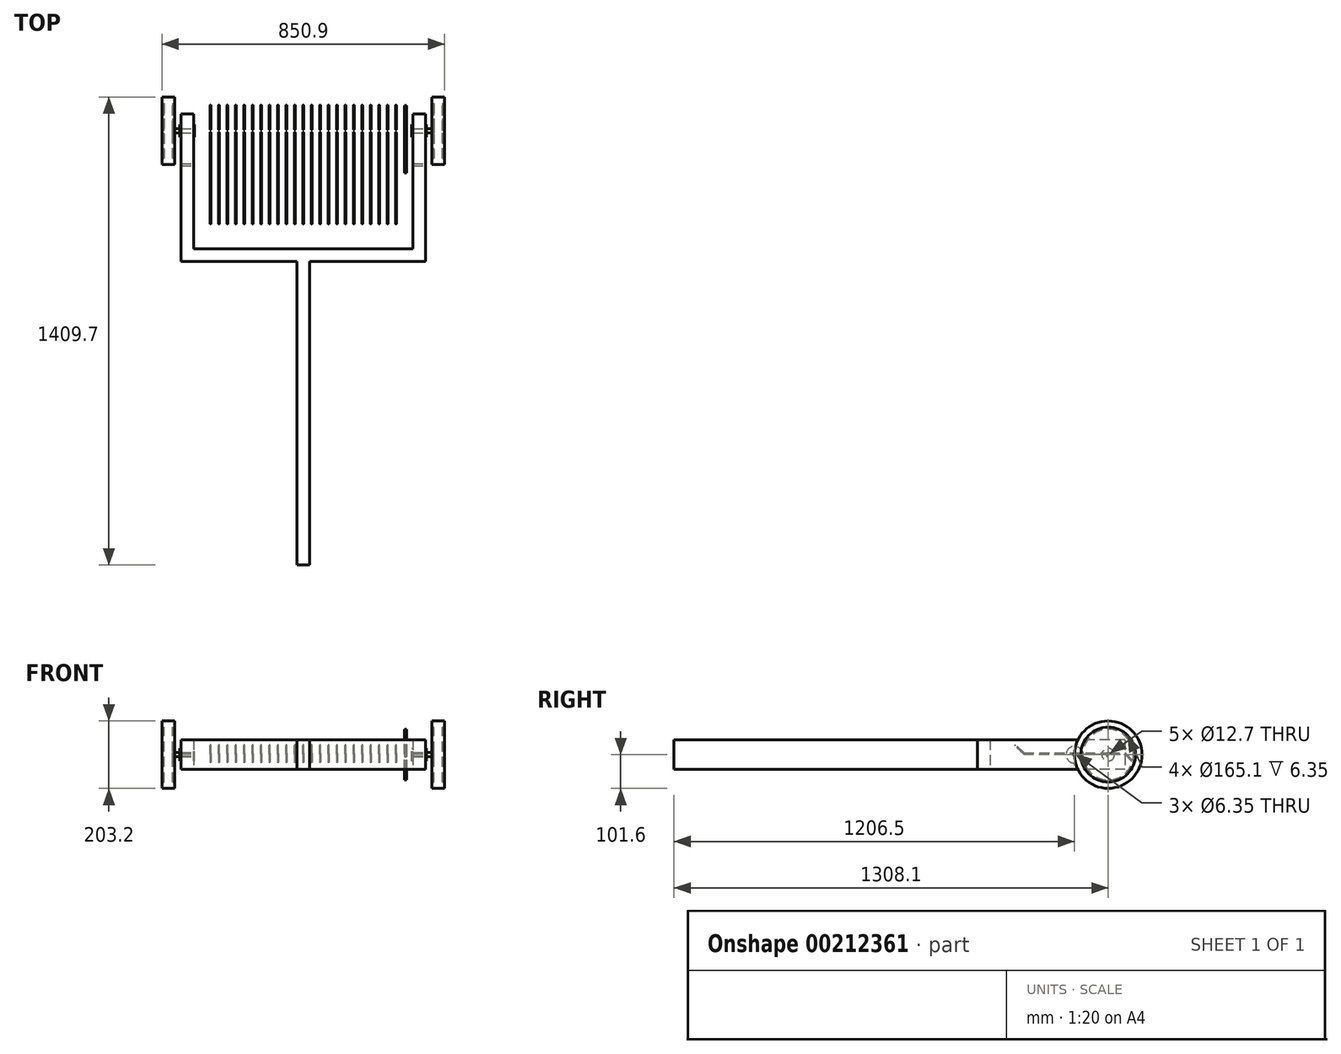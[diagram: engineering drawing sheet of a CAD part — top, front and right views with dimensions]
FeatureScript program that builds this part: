
annotation { "Feature Type Name" : "Feature", "Feature Type Description" : "" }
export const myFeature = defineFeature(function(context is Context, id is Id, definition is map)
    precondition{}
    {
        {
            var Q0;
            Q0=qCreatedBy(makeId("Top.planeOp"),FACE);
            var sketch = newSketch(context, id + "F0", { "sketchPlane" : qUnion([Q0])});
            skLineSegment(sketch, "E0.bottom", {"start": v(-368.3, 152.4) * mm, "end": v(-330.2, 152.4) * mm});
            skLineSegment(sketch, "E0.top", {"start": v(-368.3, -292.1) * mm, "end": v(-19.05, -292.1) * mm});
            skLineSegment(sketch, "E0.left", {"start": v(-368.3, 152.4) * mm, "end": v(-368.3, -292.1) * mm});
            skLineSegment(sketch, "E0.right", {"start": v(368.3, 152.4) * mm, "end": v(368.3, -292.1) * mm});
            skLineSegment(sketch, "E1.top", {"start": v(-19.05, -1206.5) * mm, "end": v(19.05, -1206.5) * mm});
            skLineSegment(sketch, "E1.left", {"start": v(-19.05, -292.1) * mm, "end": v(-19.05, -1206.5) * mm});
            skLineSegment(sketch, "E1.right", {"start": v(19.05, -292.1) * mm, "end": v(19.05, -1206.5) * mm});
            skLineSegment(sketch, "E2.top", {"start": v(-330.2, -254) * mm, "end": v(330.2, -254) * mm});
            skLineSegment(sketch, "E2.left", {"start": v(-330.2, 152.4) * mm, "end": v(-330.2, -254) * mm});
            skLineSegment(sketch, "E2.right", {"start": v(330.2, 152.4) * mm, "end": v(330.2, -254) * mm});
            skLineSegment(sketch, "E3.trimOffspring", {"start": v(330.2, 152.4) * mm, "end": v(368.3, 152.4) * mm});
            skLineSegment(sketch, "E4.trimOffspring", {"start": v(19.05, -292.1) * mm, "end": v(368.3, -292.1) * mm});
            skLineSegment(sketch, "E5", {"start": v(19.05, -292.1) * mm, "end": v(19.05, -254) * mm, "construction": true});
            skLineSegment(sketch, "E6", {"start": v(0, 0) * mm, "end": v(0, -254) * mm, "construction": true});
            skSolve(sketch);
        }
        {
            var Q0;
            Q0 = qSketchRegion(id + "F0", true);
            extrude(context, id + "F1", {"entities" : qUnion([Q0]), "endBound" : BoundingType.SYMMETRIC, "depth" : 88.9 * mm});
        }
        {
            var Q0;
            Q0=qCreatedBy(makeId("Right.planeOp"),FACE);
            var sketch = newSketch(context, id + "F2", { "sketchPlane" : qUnion([Q0])});
            skCircle(sketch, "E7", {"center": v(0, 0) * mm, "radius": 3.17 * mm});
            skSolve(sketch);
        }
        {
            var Q0;
            Q0 = qSketchRegion(id + "F2", true);
            extrude(context, id + "F3", {"entities" : qUnion([Q0]), "endBound" : BoundingType.SYMMETRIC, "depth" : 711.2 * mm});
        }
        {
            var Q0;
            Q0=qCreatedBy(makeId("Right.planeOp"),FACE);
            var sketch = newSketch(context, id + "F4", { "sketchPlane" : qUnion([Q0])});
            skLineSegment(sketch, "E8", {"start": v(-152.4, 3.17) * mm, "end": v(0, 3.17) * mm, "construction": true});
            skLineSegment(sketch, "E9", {"start": v(152.4, 3.17) * mm, "end": v(177.8, -22.22) * mm});
            skLineSegment(sketch, "E10", {"start": v(-152.4, 3.17) * mm, "end": v(-177.8, 28.58) * mm, "construction": true});
            skLineSegment(sketch, "E11", {"start": v(0, 0) * mm, "end": v(0, 3.17) * mm, "construction": true});
            skCircle(sketch, "E12.0", {"center": v(0, 0) * mm, "radius": 3.17 * mm, "construction": true});
            skLineSegment(sketch, "E13", {"start": v(-177.8, 28.58) * mm, "end": v(0, 3.17) * mm, "construction": true});
            skLineSegment(sketch, "E14", {"start": v(0, 3.17) * mm, "end": v(177.8, -22.22) * mm, "construction": true});
            skLineSegment(sketch, "E15", {"start": v(0, 3.17) * mm, "end": v(152.4, 3.17) * mm});
            skSolve(sketch);
        }
        {
            var Q0;
            Q0=qCreatedBy(makeId("Front.planeOp"),FACE);
            var sketch = newSketch(context, id + "F5", { "sketchPlane" : qUnion([Q0])});
            skCircle(sketch, "E16", {"center": v(0, 3.17) * mm, "radius": 1.59 * mm});
            skCircle(sketch, "E17.1.0.0", {"center": v(25.4, 3.17) * mm, "radius": 1.59 * mm});
            skCircle(sketch, "E17.2.0.0", {"center": v(50.8, 3.17) * mm, "radius": 1.59 * mm});
            skCircle(sketch, "E17.3.0.0", {"center": v(76.2, 3.17) * mm, "radius": 1.59 * mm});
            skCircle(sketch, "E17.4.0.0", {"center": v(101.6, 3.17) * mm, "radius": 1.59 * mm});
            skCircle(sketch, "E17.5.0.0", {"center": v(127, 3.17) * mm, "radius": 1.59 * mm});
            skCircle(sketch, "E17.6.0.0", {"center": v(152.4, 3.17) * mm, "radius": 1.59 * mm});
            skCircle(sketch, "E17.7.0.0", {"center": v(177.8, 3.17) * mm, "radius": 1.59 * mm});
            skCircle(sketch, "E17.8.0.0", {"center": v(203.2, 3.17) * mm, "radius": 1.59 * mm});
            skCircle(sketch, "E17.9.0.0", {"center": v(228.6, 3.17) * mm, "radius": 1.59 * mm});
            skCircle(sketch, "E17.10.0.0", {"center": v(254, 3.17) * mm, "radius": 1.59 * mm});
            skCircle(sketch, "E17.11.0.0", {"center": v(279.4, 3.17) * mm, "radius": 1.59 * mm});
            skLineSegment(sketch, "E17.direction1", {"start": v(0, 3.17) * mm, "end": v(25.4, 3.17) * mm, "construction": true});
            skCircle(sketch, "E18.1.0.0", {"center": v(-25.4, 3.17) * mm, "radius": 1.59 * mm});
            skCircle(sketch, "E18.2.0.0", {"center": v(-50.8, 3.17) * mm, "radius": 1.59 * mm});
            skCircle(sketch, "E18.3.0.0", {"center": v(-76.2, 3.17) * mm, "radius": 1.59 * mm});
            skCircle(sketch, "E18.4.0.0", {"center": v(-101.6, 3.17) * mm, "radius": 1.59 * mm});
            skCircle(sketch, "E18.5.0.0", {"center": v(-127, 3.17) * mm, "radius": 1.59 * mm});
            skCircle(sketch, "E18.6.0.0", {"center": v(-152.4, 3.17) * mm, "radius": 1.59 * mm});
            skCircle(sketch, "E18.7.0.0", {"center": v(-177.8, 3.17) * mm, "radius": 1.59 * mm});
            skCircle(sketch, "E18.8.0.0", {"center": v(-203.2, 3.17) * mm, "radius": 1.59 * mm});
            skCircle(sketch, "E18.9.0.0", {"center": v(-228.6, 3.17) * mm, "radius": 1.59 * mm});
            skCircle(sketch, "E18.10.0.0", {"center": v(-254, 3.17) * mm, "radius": 1.59 * mm});
            skCircle(sketch, "E18.11.0.0", {"center": v(-279.4, 3.17) * mm, "radius": 1.59 * mm});
            skLineSegment(sketch, "E18.direction1", {"start": v(0, 3.17) * mm, "end": v(-25.4, 3.17) * mm, "construction": true});
            skSolve(sketch);
        }
        {
            var Q0;
            Q0 = qSketchRegion(id + "F5", true);
            var Q1;
            Q1 = qConstructionFilter(qBodyType(qCreatedBy(id + "F4" ,EDGE), BodyType.WIRE), ConstructionObject.NO);
            sweep(context, id + "F6", {"operationType" : NewBodyOperationType.ADD, "profiles" : qUnion([Q0]), "path" : qUnion([Q1])});
        }
        {
            var Q0;
            Q0=qCreatedBy(makeId("Right.planeOp"),FACE);
            var sketch = newSketch(context, id + "F7", { "sketchPlane" : qUnion([Q0])});
            skLineSegment(sketch, "E19.0", {"start": v(-152.4, 3.17) * mm, "end": v(0, 3.17) * mm});
            skLineSegment(sketch, "E20.0", {"start": v(-152.4, 3.17) * mm, "end": v(-177.8, 28.58) * mm});
            skSolve(sketch);
        }
        {
            var Q0;
            Q0 = qSketchRegion(id + "F5", true);
            var Q1;
            Q1 = qConstructionFilter(qBodyType(qCreatedBy(id + "F7" ,EDGE), BodyType.WIRE), ConstructionObject.NO);
            sweep(context, id + "F8", {"operationType" : NewBodyOperationType.ADD, "profiles" : qUnion([Q0]), "path" : qUnion([Q1])});
        }
        {
            var Q0;
            Q0=qCreatedBy(makeId("Front.planeOp"),FACE);
            cPlane(context, id + "F9", {"entities" : qUnion([Q0]), "cplaneType" : CPlaneType.OFFSET, "offset" : 101.6 * mm, "oppositeDirection" : true, "width" : 152.4 * mm, "height" : 152.4 * mm});
        }
        {
            var Q0;
            Q0=qCreatedBy(id+"F9.planeOp",FACE);
            var sketch = newSketch(context, id + "F10", { "sketchPlane" : qUnion([Q0])});
            skLineSegment(sketch, "E21", {"start": v(419.1, 0) * mm, "end": v(-419.1, 0) * mm, "construction": true});
            skLineSegment(sketch, "E22", {"start": v(0, 0) * mm, "end": v(0, 115.83) * mm, "construction": true});
            skLineSegment(sketch, "E23.0", {"start": v(368.3, 44.45) * mm, "end": v(368.3, -44.45) * mm, "construction": true});
            skLineSegment(sketch, "E24.bottom", {"start": v(425.45, 101.6) * mm, "end": v(387.35, 101.6) * mm});
            skLineSegment(sketch, "E24.top", {"start": v(425.45, 82.55) * mm, "end": v(419.1, 82.55) * mm});
            skLineSegment(sketch, "E24.left", {"start": v(425.45, 101.6) * mm, "end": v(425.45, 82.55) * mm});
            skLineSegment(sketch, "E24.right", {"start": v(387.35, 101.6) * mm, "end": v(387.35, 82.55) * mm});
            skLineSegment(sketch, "E25.bottom", {"start": v(419.1, 0) * mm, "end": v(393.7, 0) * mm});
            skLineSegment(sketch, "E25.left", {"start": v(419.1, 0) * mm, "end": v(419.1, 82.55) * mm});
            skLineSegment(sketch, "E25.right", {"start": v(393.7, 6.35) * mm, "end": v(393.7, 82.55) * mm});
            skLineSegment(sketch, "E26.trimOffspring", {"start": v(393.7, 82.55) * mm, "end": v(387.35, 82.55) * mm});
            skLineSegment(sketch, "E27.MirrorCS", {"start": v(-425.45, 82.55) * mm, "end": v(-419.1, 82.55) * mm});
            skLineSegment(sketch, "E28.MirrorCS", {"start": v(-393.7, 82.55) * mm, "end": v(-387.35, 82.55) * mm});
            skLineSegment(sketch, "E29.MirrorCS", {"start": v(-419.1, 0) * mm, "end": v(-393.7, 0) * mm});
            skLineSegment(sketch, "E30.MirrorCS", {"start": v(-393.7, 6.35) * mm, "end": v(-393.7, 82.55) * mm});
            skLineSegment(sketch, "E31.MirrorCS", {"start": v(-387.35, 101.6) * mm, "end": v(-387.35, 82.55) * mm});
            skLineSegment(sketch, "E32.MirrorCS", {"start": v(-425.45, 101.6) * mm, "end": v(-387.35, 101.6) * mm});
            skLineSegment(sketch, "E33.MirrorCS", {"start": v(-425.45, 101.6) * mm, "end": v(-425.45, 82.55) * mm});
            skLineSegment(sketch, "E34.MirrorCS", {"start": v(-419.1, 0) * mm, "end": v(-419.1, 82.55) * mm});
            skLineSegment(sketch, "E35.bottom", {"start": v(393.7, 0) * mm, "end": v(304.8, 0) * mm});
            skLineSegment(sketch, "E35.top", {"start": v(393.7, 6.35) * mm, "end": v(371.47, 6.35) * mm});
            skLineSegment(sketch, "E35.right", {"start": v(304.8, 0) * mm, "end": v(304.8, 6.35) * mm});
            skLineSegment(sketch, "E36.top", {"start": v(371.47, 19.05) * mm, "end": v(368.3, 19.05) * mm});
            skLineSegment(sketch, "E36.left", {"start": v(371.47, 6.35) * mm, "end": v(371.47, 19.05) * mm});
            skLineSegment(sketch, "E36.right", {"start": v(368.3, 6.35) * mm, "end": v(368.3, 19.05) * mm});
            skLineSegment(sketch, "E37.top", {"start": v(330.2, 19.05) * mm, "end": v(327.03, 19.05) * mm});
            skLineSegment(sketch, "E37.left", {"start": v(330.2, 6.35) * mm, "end": v(330.2, 19.05) * mm});
            skLineSegment(sketch, "E37.right", {"start": v(327.03, 6.35) * mm, "end": v(327.03, 19.05) * mm});
            skLineSegment(sketch, "E38.trimOffspring", {"start": v(327.03, 6.35) * mm, "end": v(304.8, 6.35) * mm});
            skLineSegment(sketch, "E39.trimOffspring", {"start": v(368.3, 6.35) * mm, "end": v(330.2, 6.35) * mm});
            skLineSegment(sketch, "E40.MirrorCS", {"start": v(-371.47, 19.05) * mm, "end": v(-368.3, 19.05) * mm});
            skLineSegment(sketch, "E41.MirrorCS", {"start": v(-304.8, 0) * mm, "end": v(-304.8, 6.35) * mm});
            skLineSegment(sketch, "E42.MirrorCS", {"start": v(-330.2, 19.05) * mm, "end": v(-327.03, 19.05) * mm});
            skLineSegment(sketch, "E43.MirrorCS", {"start": v(-368.3, 6.35) * mm, "end": v(-368.3, 19.05) * mm});
            skLineSegment(sketch, "E44.MirrorCS", {"start": v(-393.7, 6.35) * mm, "end": v(-371.47, 6.35) * mm});
            skLineSegment(sketch, "E45.MirrorCS", {"start": v(-393.7, 0) * mm, "end": v(-304.8, 0) * mm});
            skLineSegment(sketch, "E46.MirrorCS", {"start": v(-371.47, 6.35) * mm, "end": v(-371.47, 19.05) * mm});
            skLineSegment(sketch, "E47.MirrorCS", {"start": v(-330.2, 6.35) * mm, "end": v(-330.2, 19.05) * mm});
            skLineSegment(sketch, "E48.MirrorCS", {"start": v(-327.03, 6.35) * mm, "end": v(-304.8, 6.35) * mm});
            skLineSegment(sketch, "E49.MirrorCS", {"start": v(-327.03, 6.35) * mm, "end": v(-327.03, 19.05) * mm});
            skLineSegment(sketch, "E50.MirrorCS", {"start": v(-368.3, 6.35) * mm, "end": v(-330.2, 6.35) * mm});
            skSolve(sketch);
        }
        {
            var Q0;
            Q0 = qSketchRegion(id + "F10", true);
            var Q1;
            Q1=sQuery(id+"F10.wireOp",EDGE,"E21");
            revolve(context, id + "F11", {"entities" : qUnion([Q0]), "axis" : qUnion([Q1]), "revolveType" : RevolveType.FULL});
        }
        {
            var Q0;
            Q0=makeQuery(id+"F11.opRevolve","SWEPT_FACE",FACE,{"disambiguationData":[OSD([sQuery(id+"F10.wireOp",EDGE,"E35.right")])]});
            var sketch = newSketch(context, id + "F12", { "sketchPlane" : qUnion([Q0])});
            skCircle(sketch, "E51", {"center": v(-101.6, 0) * mm, "radius": 76.2 * mm});
            skCircle(sketch, "E52.0", {"center": v(0, 0) * mm, "radius": 3.17 * mm, "construction": true});
            skCircle(sketch, "E53", {"center": v(0, 0) * mm, "radius": 25.4 * mm});
            skSolve(sketch);
        }
        {
            var Q0;
            Q0 = qSketchRegion(id + "F12", true);
            extrude(context, id + "F13", {"entities" : qUnion([Q0]), "oppositeDirection" : true, "depth" : 6.35 * mm});
        }
        {
            var Q0;
            Q0=qCreatedBy(makeId("Right.planeOp"),FACE);
            var sketch = newSketch(context, id + "F14", { "sketchPlane" : qUnion([Q0])});
            skCircle(sketch, "E54.0", {"center": v(0, 0) * mm, "radius": 3.17 * mm});
            skCircle(sketch, "E55.0", {"center": v(101.6, 0) * mm, "radius": 6.35 * mm});
            skSolve(sketch);
        }
        {
            var Q0;
            Q0 = qSketchRegion(id + "F14", true);
            var Q1;
            Q1=makeQuery(id+"F1.opExtrude","SWEPT_FACE",FACE,{"disambiguationData":[OSD([sQuery(id+"F0.wireOp",EDGE,"E0.left")])]});
            var Q2;
            Q2=makeQuery(id+"F1.opExtrude","SWEPT_FACE",FACE,{"disambiguationData":[OSD([sQuery(id+"F0.wireOp",EDGE,"E0.right")])]});
            extrude(context, id + "F15", {"entities" : qUnion([Q0]), "operationType" : NewBodyOperationType.REMOVE, "endBound" : BoundingType.UP_TO_SURFACE, "oppositeDirection" : true, "endBoundEntityFace" : qUnion([Q1]), "depth" : 25.4 * mm, "hasSecondDirection" : true, "secondDirectionBound" : SecondDirectionBoundingType.UP_TO_SURFACE, "secondDirectionOppositeDirection" : false, "secondDirectionBoundEntityFace" : qUnion([Q2]), "secondDirectionDepth" : 25.4 * mm});
        }
    });
